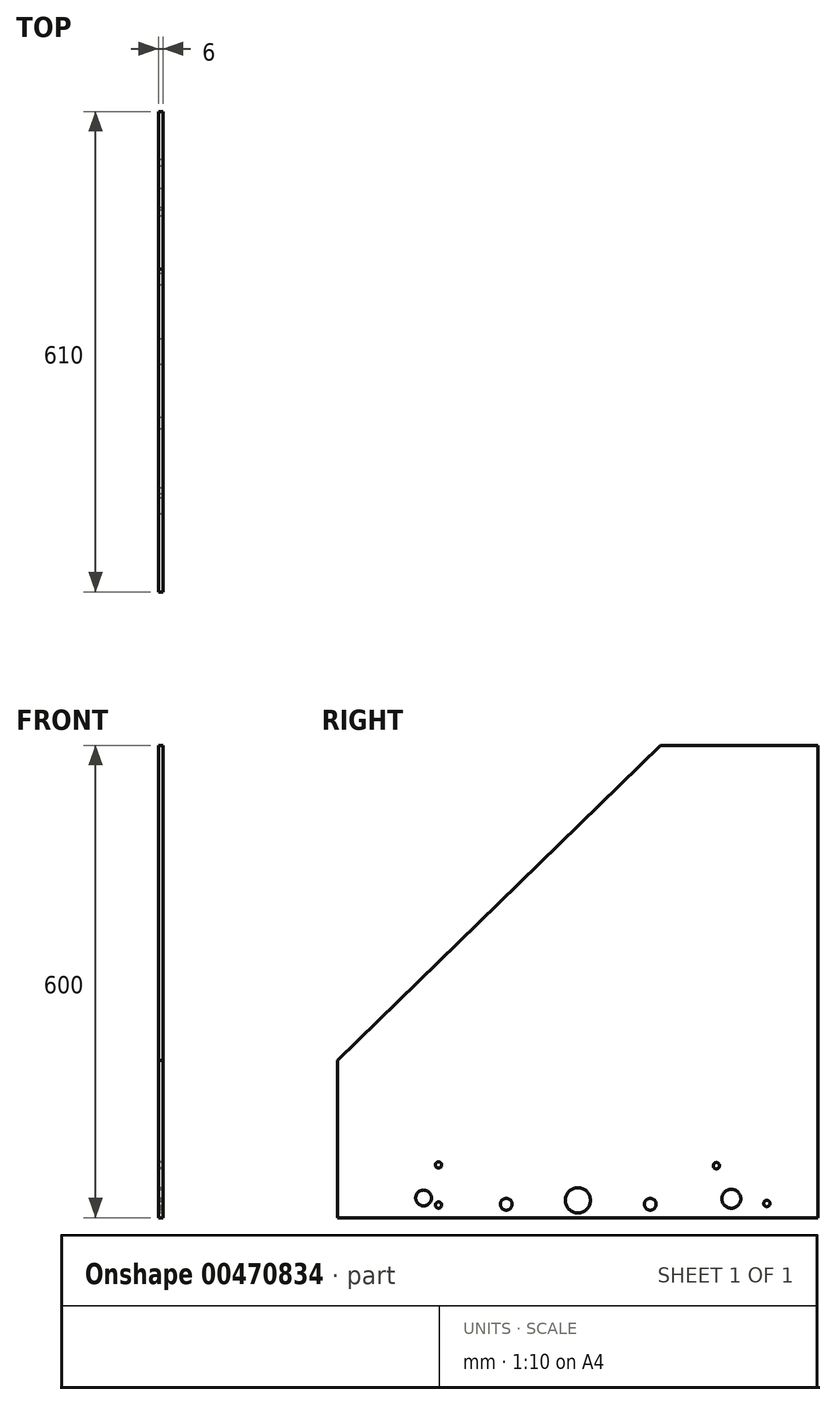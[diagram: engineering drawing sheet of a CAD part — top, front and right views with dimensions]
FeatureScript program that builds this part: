
annotation { "Feature Type Name" : "Feature", "Feature Type Description" : "" }
export const myFeature = defineFeature(function(context is Context, id is Id, definition is map)
    precondition{}
    {
        {
            var Q0;
            Q0=qCreatedBy(makeId("Right.planeOp"),FACE);
            var sketch = newSketch(context, id + "F0", { "sketchPlane" : qUnion([Q0])});
            skLineSegment(sketch, "E0", {"start": v(0, 0) * mm, "end": v(-610, 0) * mm});
            skLineSegment(sketch, "E1", {"start": v(-610, 0) * mm, "end": v(-610, 200) * mm});
            skLineSegment(sketch, "E2", {"start": v(0, 0) * mm, "end": v(0, 600) * mm});
            skLineSegment(sketch, "E3", {"start": v(0, 600) * mm, "end": v(-200, 600) * mm});
            skLineSegment(sketch, "E4", {"start": v(-610, 200) * mm, "end": v(-200, 600) * mm});
            skCircle(sketch, "E5", {"center": v(-65, 18) * mm, "radius": 4 * mm});
            skCircle(sketch, "E6", {"center": v(-110, 24) * mm, "radius": 12 * mm});
            skCircle(sketch, "E7", {"center": v(-129, 66) * mm, "radius": 4 * mm});
            skCircle(sketch, "E8", {"center": v(-213, 17) * mm, "radius": 7.5 * mm});
            skCircle(sketch, "E9", {"center": v(-305, 22) * mm, "radius": 16 * mm});
            skCircle(sketch, "E10", {"center": v(-396, 17) * mm, "radius": 7.5 * mm});
            skCircle(sketch, "E11", {"center": v(-482, 67) * mm, "radius": 4 * mm});
            skCircle(sketch, "E12", {"center": v(-482, 16) * mm, "radius": 4 * mm});
            skLineSegment(sketch, "E13", {"start": v(0, 0) * mm, "end": v(-496, 0) * mm});
            skCircle(sketch, "E14", {"center": v(-501, 25) * mm, "radius": 10 * mm});
            skSolve(sketch);
        }
        {
            var Q0;
            Q0=makeQuery(id+"F0.imprint","IMPRINT",FACE,{"disambiguationData":[TD([[makeQuery(id+"F0.imprint","IMPRINT",EDGE,{"derivedFrom":sQuery(id+"F0.wireOp",EDGE,"E0")}),-1.0]])]});
            extrude(context, id + "F1", {"entities" : qUnion([Q0]), "depth" : 6 * mm});
        }
    });
